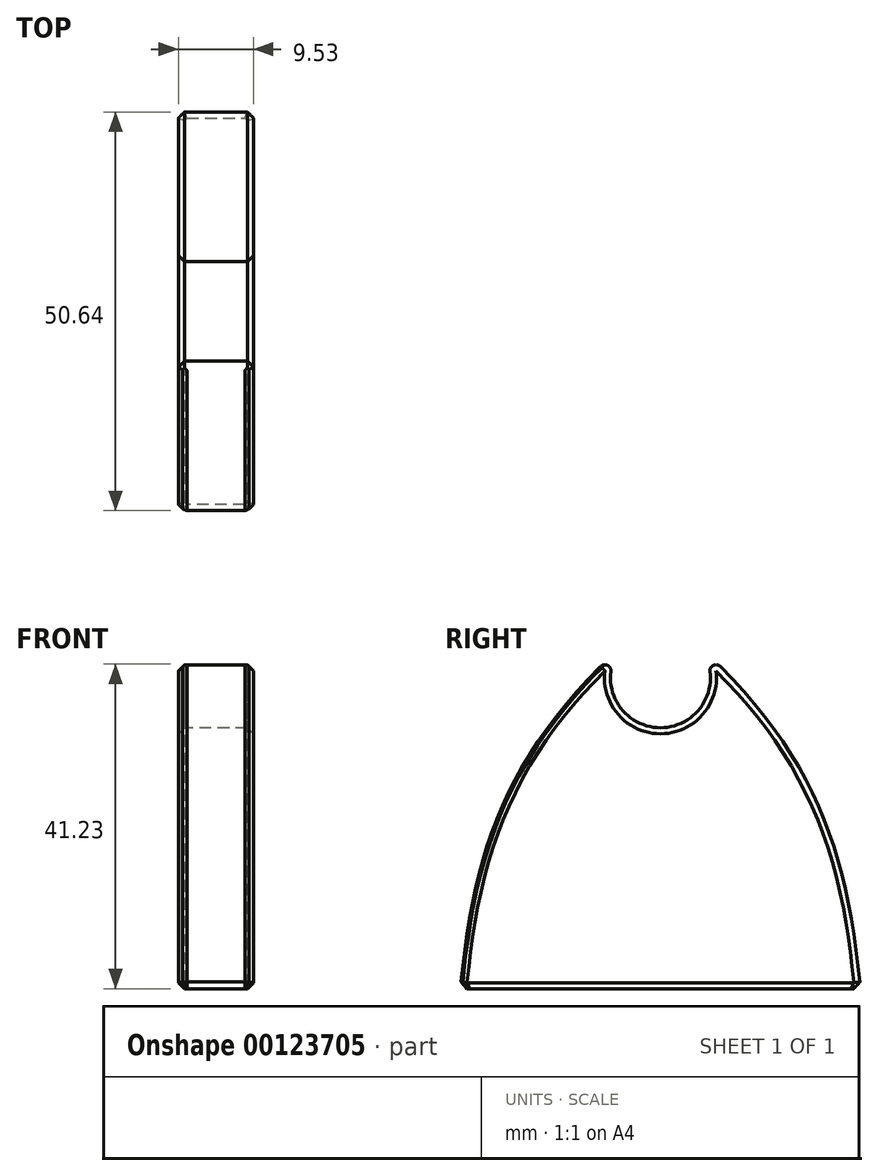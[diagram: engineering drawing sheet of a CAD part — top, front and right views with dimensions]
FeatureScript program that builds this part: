
annotation { "Feature Type Name" : "Feature", "Feature Type Description" : "" }
export const myFeature = defineFeature(function(context is Context, id is Id, definition is map)
    precondition{}
    {
        {
            var Q0;
            Q0=qCreatedBy(makeId("Right.planeOp"),FACE);
            var sketch = newSketch(context, id + "F0", { "sketchPlane" : qUnion([Q0])});
            skArc(sketch, "E0", {"start": v(-44.92, 21.97) * mm, "mid": v(-38.62, 14.82) * mm, "end": v(-32.32, 21.97) * mm});
            skLineSegment(sketch, "E1", {"start": v(-64.02, -18.33) * mm, "end": v(-13.22, -18.33) * mm});
            skFitSpline(sketch, "E2", {"points": [v(-42.14, 26.45) * mm, v(-64.02, -18.33) * mm], "startDerivative": vector(-46.76, -41.68) * mm, "endDerivative": vector(-4.92, -55) * mm});
            skFitSpline(sketch, "E3.MirrorCS", {"points": [v(-35.1, 26.45) * mm, v(-13.22, -18.33) * mm], "startDerivative": vector(46.76, -41.68) * mm, "endDerivative": vector(4.92, -55) * mm});
            skArc(sketch, "E4.filletArc", {"start": v(-44.92, 21.97) * mm, "mid": v(-45.34, 22.75) * mm, "end": v(-46.22, 22.6) * mm});
            skArc(sketch, "E5.filletArc", {"start": v(-31.03, 22.6) * mm, "mid": v(-31.9, 22.75) * mm, "end": v(-32.32, 21.97) * mm});
            skSolve(sketch);
        }
        {
            var Q0;
            Q0=makeQuery(id+"F0.imprint","IMPRINT",FACE,{"disambiguationData":[TD([[makeQuery(id+"F0.imprint","IMPRINT",EDGE,{"derivedFrom":sQuery(id+"F0.wireOp",EDGE,"E0")}),-1.0]])]});
            extrude(context, id + "F1", {"entities" : qUnion([Q0]), "depth" : 9.52 * mm});
        }
        {
            var Q0;
            Q0=makeQuery(id+"F1.opExtrude","CAP_EDGE",EDGE,{"disambiguationData":[OSD([sQuery(id+"F0.wireOp",EDGE,"E2")])],"isStart":true});
            var Q1;
            Q1=makeQuery(id+"F1.opExtrude","CAP_EDGE",EDGE,{"disambiguationData":[OSD([sQuery(id+"F0.wireOp",EDGE,"E2")])],"isStart":false});
            chamfer(context, id + "F2", {"entities" : qUnion([Q0, Q1]), "width" : 0.76 * mm, "tangentPropagation" : true});
        }
        {
            var Q0;
            Q0=makeQuery(id+"F1.opExtrude","SWEPT_FACE",FACE,{"disambiguationData":[OSD([sQuery(id+"F0.wireOp",EDGE,"E1")])]});
            var Q1;
            Q1=makeQuery(id+"F1.opExtrude","SWEPT_FACE",FACE,{"disambiguationData":[OSD([sQuery(id+"F0.wireOp",EDGE,"E2")])]});
            chamfer(context, id + "F3", {"entities" : qUnion([Q0, Q1]), "width" : 0.76 * mm, "tangentPropagation" : true});
        }
    });
